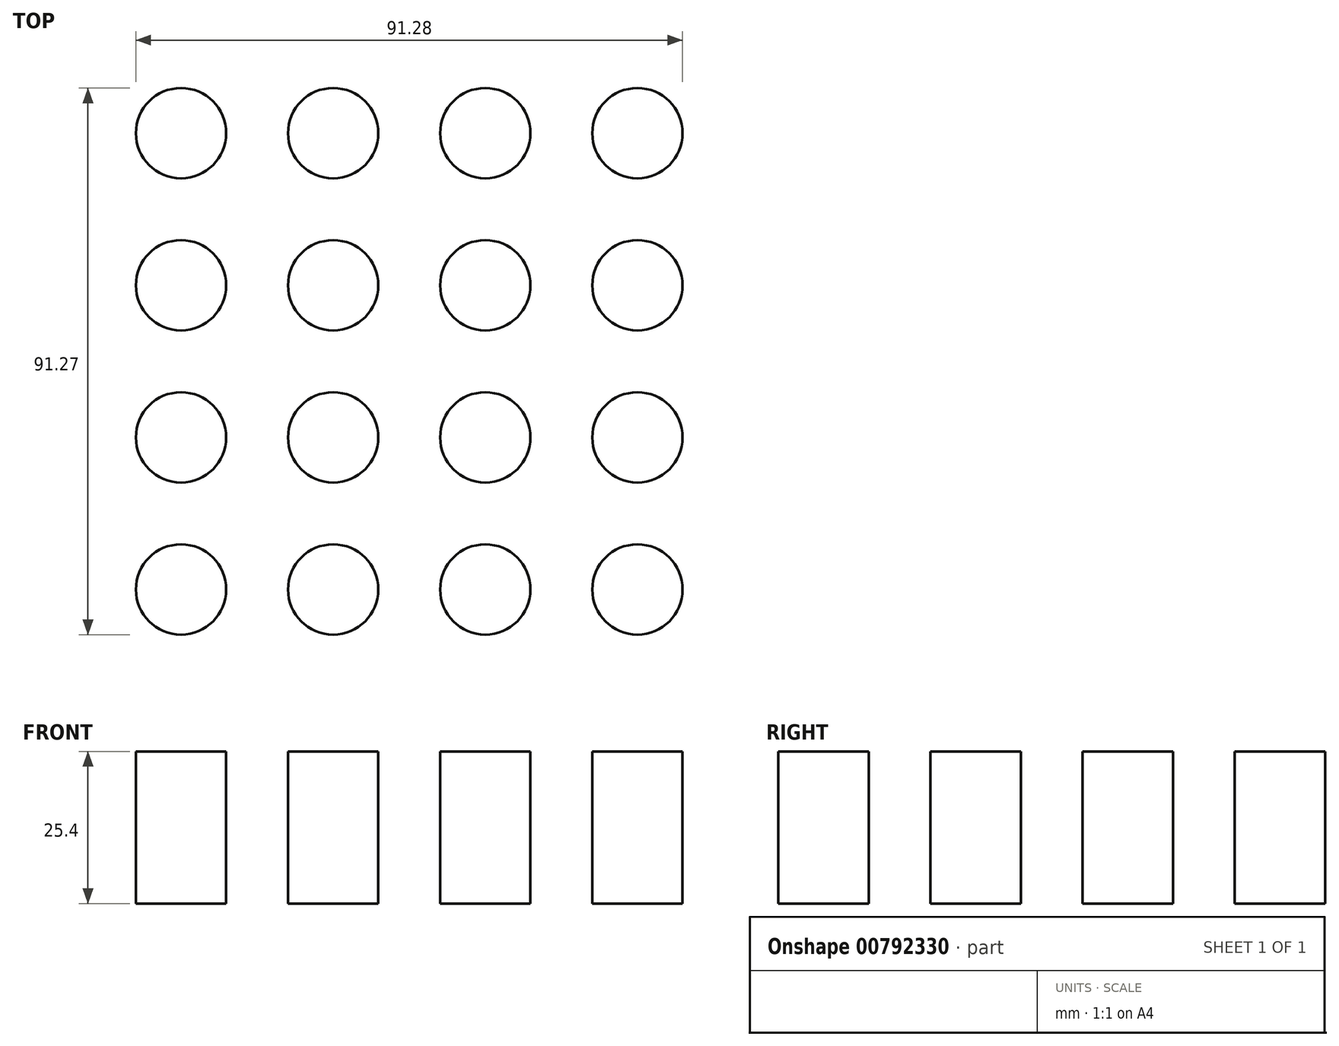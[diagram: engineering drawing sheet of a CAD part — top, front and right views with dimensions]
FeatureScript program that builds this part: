
annotation { "Feature Type Name" : "Feature", "Feature Type Description" : "" }
export const myFeature = defineFeature(function(context is Context, id is Id, definition is map)
    precondition{}
    {
        {
            var Q0;
            Q0=qCreatedBy(makeId("Top.planeOp"),FACE);
            var sketch = newSketch(context, id + "F0", { "sketchPlane" : qUnion([Q0])});
            skCircle(sketch, "E0", {"center": v(-54.69, 50.97) * mm, "radius": 7.54 * mm});
            skCircle(sketch, "E1.0.1.0", {"center": v(-54.69, 25.57) * mm, "radius": 7.54 * mm});
            skCircle(sketch, "E1.0.2.0", {"center": v(-54.69, 0.17) * mm, "radius": 7.54 * mm});
            skCircle(sketch, "E1.0.3.0", {"center": v(-54.69, -25.23) * mm, "radius": 7.54 * mm});
            skCircle(sketch, "E1.1.0.0", {"center": v(-29.29, 50.97) * mm, "radius": 7.54 * mm});
            skCircle(sketch, "E1.1.1.0", {"center": v(-29.29, 25.57) * mm, "radius": 7.54 * mm});
            skCircle(sketch, "E1.1.2.0", {"center": v(-29.29, 0.17) * mm, "radius": 7.54 * mm});
            skCircle(sketch, "E1.1.3.0", {"center": v(-29.29, -25.23) * mm, "radius": 7.54 * mm});
            skCircle(sketch, "E1.2.0.0", {"center": v(-3.89, 50.97) * mm, "radius": 7.54 * mm});
            skCircle(sketch, "E1.2.1.0", {"center": v(-3.89, 25.57) * mm, "radius": 7.54 * mm});
            skCircle(sketch, "E1.2.2.0", {"center": v(-3.89, 0.17) * mm, "radius": 7.54 * mm});
            skCircle(sketch, "E1.2.3.0", {"center": v(-3.89, -25.23) * mm, "radius": 7.54 * mm});
            skCircle(sketch, "E1.3.0.0", {"center": v(21.51, 50.97) * mm, "radius": 7.54 * mm});
            skCircle(sketch, "E1.3.1.0", {"center": v(21.51, 25.57) * mm, "radius": 7.54 * mm});
            skCircle(sketch, "E1.3.2.0", {"center": v(21.51, 0.17) * mm, "radius": 7.54 * mm});
            skCircle(sketch, "E1.3.3.0", {"center": v(21.51, -25.23) * mm, "radius": 7.54 * mm});
            skLineSegment(sketch, "E1.direction1", {"start": v(-54.69, 50.97) * mm, "end": v(-29.29, 50.97) * mm, "construction": true});
            skLineSegment(sketch, "E1.direction2", {"start": v(-54.69, 50.97) * mm, "end": v(-54.69, 25.57) * mm, "construction": true});
            skSolve(sketch);
        }
        {
            var Q0;
            Q0=makeQuery(id+"F0.imprint","IMPRINT",FACE,{"disambiguationData":[TD([[makeQuery(id+"F0.imprint","IMPRINT",EDGE,{"derivedFrom":sQuery(id+"F0.wireOp",EDGE,"E1.3.0.0")}),1.0]])]});
            var Q1;
            Q1=makeQuery(id+"F0.imprint","IMPRINT",FACE,{"disambiguationData":[TD([[makeQuery(id+"F0.imprint","IMPRINT",EDGE,{"derivedFrom":sQuery(id+"F0.wireOp",EDGE,"E1.3.1.0")}),1.0]])]});
            var Q2;
            Q2=makeQuery(id+"F0.imprint","IMPRINT",FACE,{"disambiguationData":[TD([[makeQuery(id+"F0.imprint","IMPRINT",EDGE,{"derivedFrom":sQuery(id+"F0.wireOp",EDGE,"E1.3.2.0")}),1.0]])]});
            var Q3;
            Q3=makeQuery(id+"F0.imprint","IMPRINT",FACE,{"disambiguationData":[TD([[makeQuery(id+"F0.imprint","IMPRINT",EDGE,{"derivedFrom":sQuery(id+"F0.wireOp",EDGE,"E1.3.3.0")}),1.0]])]});
            var Q4;
            Q4=makeQuery(id+"F0.imprint","IMPRINT",FACE,{"disambiguationData":[TD([[makeQuery(id+"F0.imprint","IMPRINT",EDGE,{"derivedFrom":sQuery(id+"F0.wireOp",EDGE,"E1.2.3.0")}),1.0]])]});
            var Q5;
            Q5=makeQuery(id+"F0.imprint","IMPRINT",FACE,{"disambiguationData":[TD([[makeQuery(id+"F0.imprint","IMPRINT",EDGE,{"derivedFrom":sQuery(id+"F0.wireOp",EDGE,"E1.2.2.0")}),1.0]])]});
            var Q6;
            Q6=makeQuery(id+"F0.imprint","IMPRINT",FACE,{"disambiguationData":[TD([[makeQuery(id+"F0.imprint","IMPRINT",EDGE,{"derivedFrom":sQuery(id+"F0.wireOp",EDGE,"E1.2.1.0")}),1.0]])]});
            var Q7;
            Q7=makeQuery(id+"F0.imprint","IMPRINT",FACE,{"disambiguationData":[TD([[makeQuery(id+"F0.imprint","IMPRINT",EDGE,{"derivedFrom":sQuery(id+"F0.wireOp",EDGE,"E1.2.0.0")}),1.0]])]});
            var Q8;
            Q8=makeQuery(id+"F0.imprint","IMPRINT",FACE,{"disambiguationData":[TD([[makeQuery(id+"F0.imprint","IMPRINT",EDGE,{"derivedFrom":sQuery(id+"F0.wireOp",EDGE,"E1.1.0.0")}),1.0]])]});
            var Q9;
            Q9=makeQuery(id+"F0.imprint","IMPRINT",FACE,{"disambiguationData":[TD([[makeQuery(id+"F0.imprint","IMPRINT",EDGE,{"derivedFrom":sQuery(id+"F0.wireOp",EDGE,"E1.1.1.0")}),1.0]])]});
            var Q10;
            Q10=makeQuery(id+"F0.imprint","IMPRINT",FACE,{"disambiguationData":[TD([[makeQuery(id+"F0.imprint","IMPRINT",EDGE,{"derivedFrom":sQuery(id+"F0.wireOp",EDGE,"E1.1.2.0")}),1.0]])]});
            var Q11;
            Q11=makeQuery(id+"F0.imprint","IMPRINT",FACE,{"disambiguationData":[TD([[makeQuery(id+"F0.imprint","IMPRINT",EDGE,{"derivedFrom":sQuery(id+"F0.wireOp",EDGE,"E1.1.3.0")}),1.0]])]});
            var Q12;
            Q12=makeQuery(id+"F0.imprint","IMPRINT",FACE,{"disambiguationData":[TD([[makeQuery(id+"F0.imprint","IMPRINT",EDGE,{"derivedFrom":sQuery(id+"F0.wireOp",EDGE,"E1.0.2.0")}),1.0]])]});
            var Q13;
            Q13=makeQuery(id+"F0.imprint","IMPRINT",FACE,{"disambiguationData":[TD([[makeQuery(id+"F0.imprint","IMPRINT",EDGE,{"derivedFrom":sQuery(id+"F0.wireOp",EDGE,"E1.0.1.0")}),1.0]])]});
            var Q14;
            Q14=makeQuery(id+"F0.imprint","IMPRINT",FACE,{"disambiguationData":[TD([[makeQuery(id+"F0.imprint","IMPRINT",EDGE,{"derivedFrom":sQuery(id+"F0.wireOp",EDGE,"E0")}),1.0]])]});
            var Q15;
            Q15=makeQuery(id+"F0.imprint","IMPRINT",FACE,{"disambiguationData":[TD([[makeQuery(id+"F0.imprint","IMPRINT",EDGE,{"derivedFrom":sQuery(id+"F0.wireOp",EDGE,"E1.0.3.0")}),1.0]])]});
            extrude(context, id + "F1", {"entities" : qUnion([Q0, Q1, Q2, Q3, Q4, Q5, Q6, Q7, Q8, Q9, Q10, Q11, Q12, Q13, Q14, Q15]), "depth" : 25.4 * mm, "offsetDistance" : 25.4 * mm});
        }
    });
